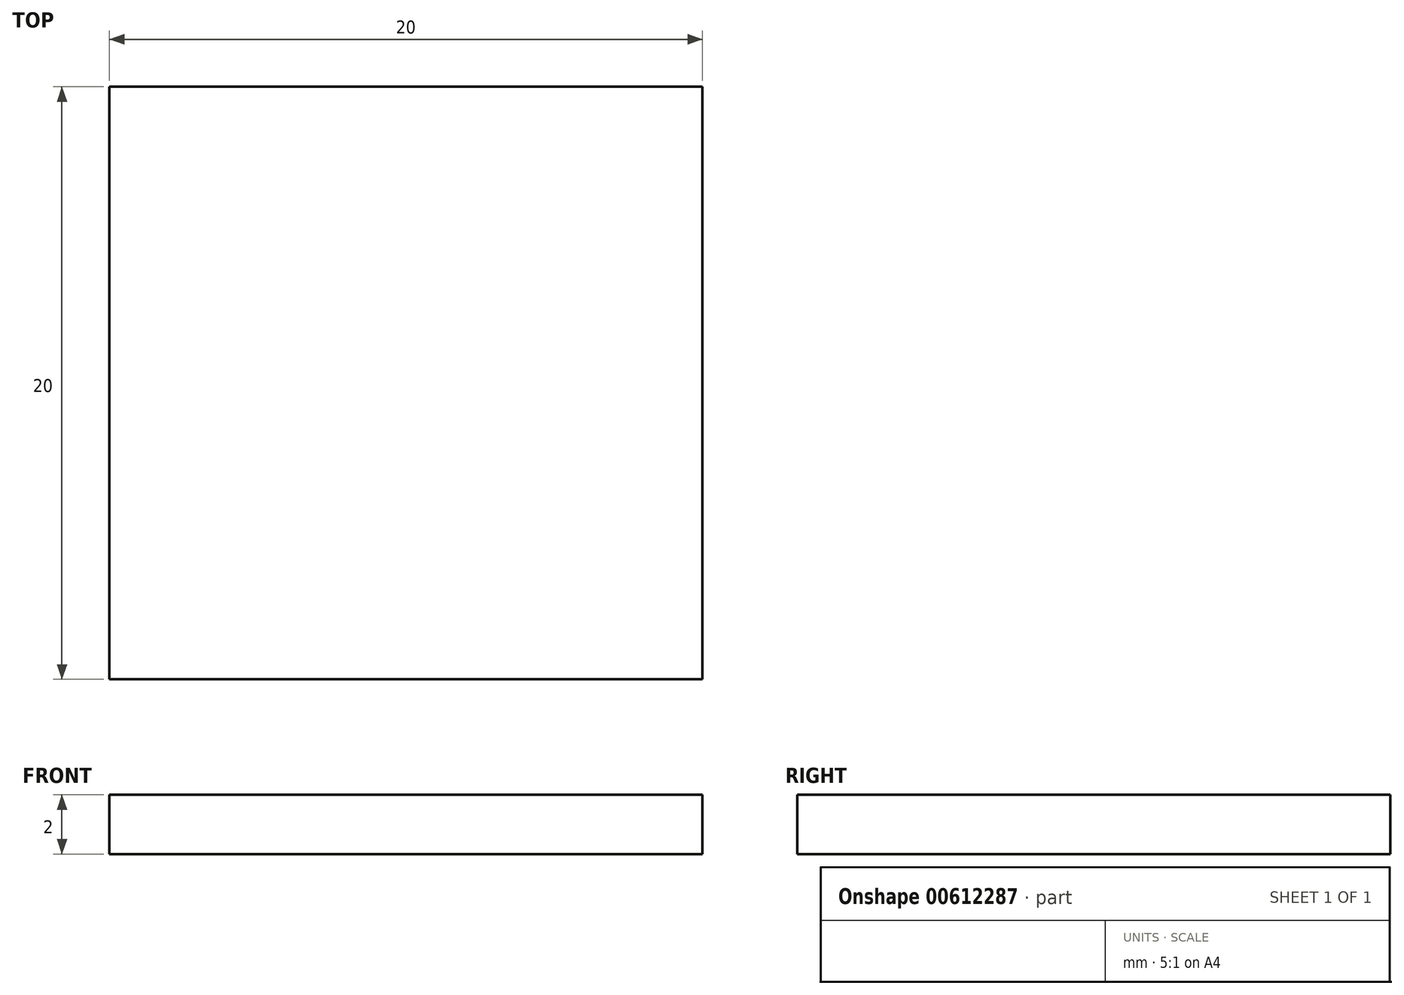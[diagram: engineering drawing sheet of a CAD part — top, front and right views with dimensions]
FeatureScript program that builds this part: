
annotation { "Feature Type Name" : "Feature", "Feature Type Description" : "" }
export const myFeature = defineFeature(function(context is Context, id is Id, definition is map)
    precondition{}
    {
        {
            var Q0;
            Q0=qCreatedBy(makeId("Top.planeOp"),FACE);
            var sketch = newSketch(context, id + "F0", { "sketchPlane" : qUnion([Q0])});
            skLineSegment(sketch, "E0.bottom", {"start": v(-0.27, 11.84) * mm, "end": v(19.73, 11.84) * mm});
            skLineSegment(sketch, "E0.top", {"start": v(-0.27, -8.16) * mm, "end": v(19.73, -8.16) * mm});
            skLineSegment(sketch, "E0.left", {"start": v(-0.27, 11.84) * mm, "end": v(-0.27, -8.16) * mm});
            skLineSegment(sketch, "E0.right", {"start": v(19.73, 11.84) * mm, "end": v(19.73, -8.16) * mm});
            skSolve(sketch);
        }
        {
            var Q0;
            Q0=qSketchRegion(id+"F0",true);
            extrude(context, id + "F1", {"entities" : qUnion([Q0]), "depth" : 2 * mm});
        }
    });
